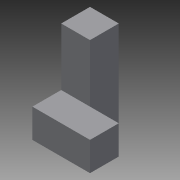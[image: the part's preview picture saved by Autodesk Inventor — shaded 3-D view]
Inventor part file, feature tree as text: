
AUTODESK INVENTOR PART (.ipt)
format: ipt  version: 2015 (Build 190159000, 159)  size: 79,360 bytes
history: native  units: in
note: dims shown in document units (in); Inventor stores cm internally (conversion verified against a paired STEP export)
features: extrude x2, sketch x2
ambient origin geometry x8: Origin, YZ Plane, XZ Plane, XY Plane, X Axis, Y Axis, Z Axis, Center Point
bodies: Solid1 (feature_tree)
feature tree (4):
  extrude  "Extrusion1"  Depth=0.75in
  extrude  "Extrusion2"  Depth=1.5in
  sketch  "Sketch1"  dims[d0=2.25in d1=0.75in]
  sketch  "Sketch2"  dims[d2=0.75in d3=0.0in d4=1.5in d5=0.75in d6=0.75in d7=0.0in]
